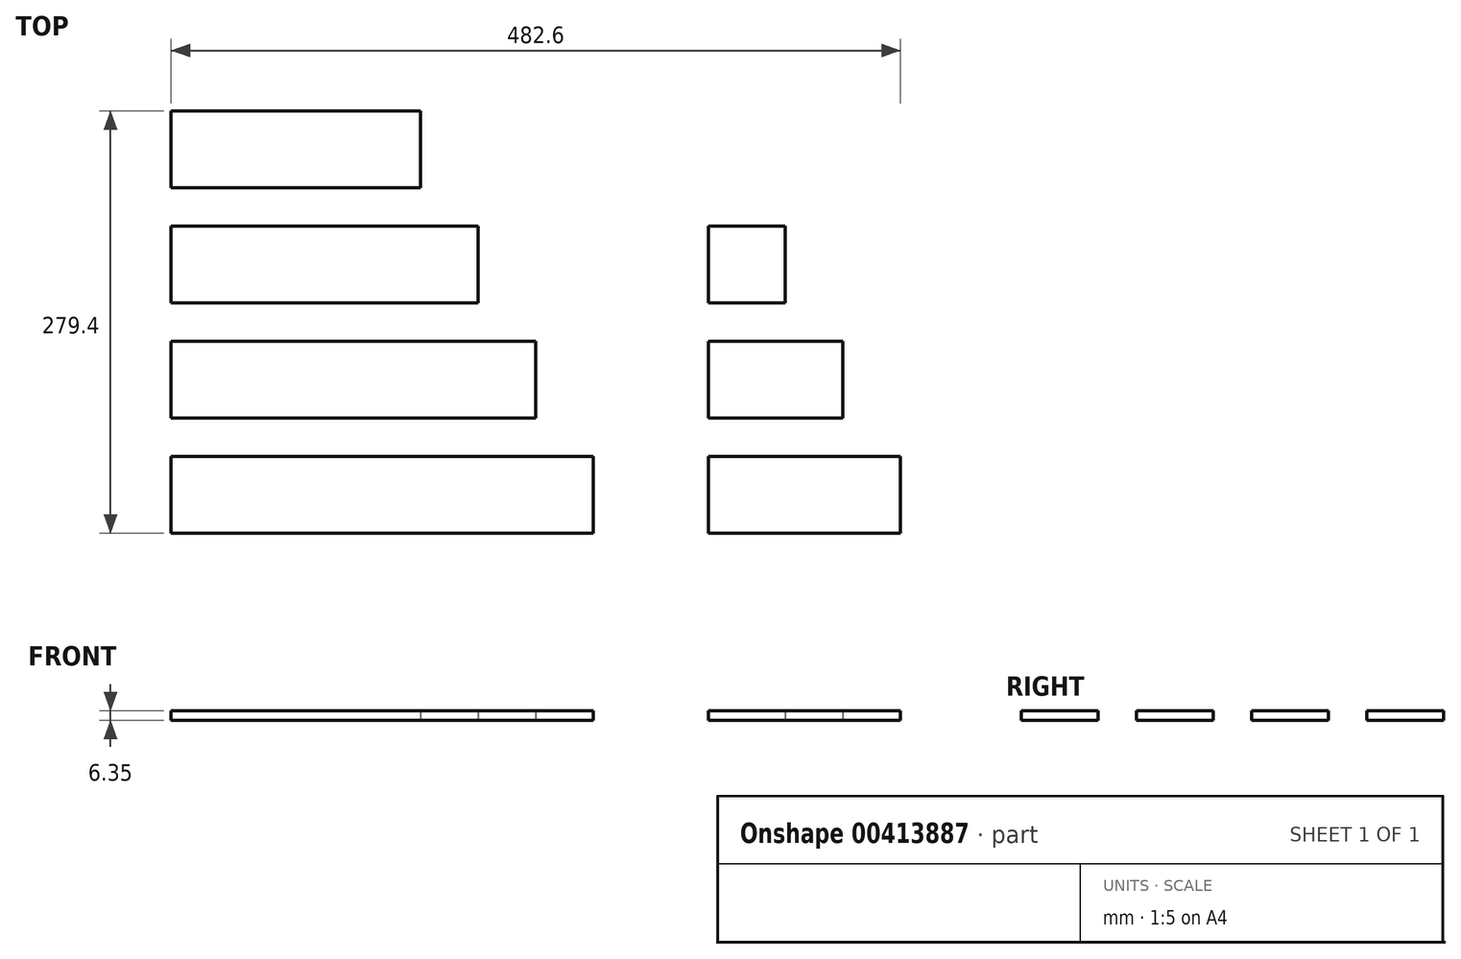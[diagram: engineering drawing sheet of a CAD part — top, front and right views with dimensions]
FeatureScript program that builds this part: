
annotation { "Feature Type Name" : "Feature", "Feature Type Description" : "" }
export const myFeature = defineFeature(function(context is Context, id is Id, definition is map)
    precondition{}
    {
        {
            var Q0;
            Q0=qCreatedBy(makeId("Top.planeOp"),FACE);
            var sketch = newSketch(context, id + "F0", { "sketchPlane" : qUnion([Q0])});
            skLineSegment(sketch, "E0.bottom", {"start": v(0, 38.1) * mm, "end": v(266.7, 38.1) * mm});
            skLineSegment(sketch, "E0.top", {"start": v(0, 0) * mm, "end": v(266.7, 0) * mm});
            skLineSegment(sketch, "E0.left", {"start": v(0, 38.1) * mm, "end": v(0, 0) * mm});
            skLineSegment(sketch, "E0.right", {"start": v(266.7, 38.1) * mm, "end": v(266.7, 0) * mm});
            skLineSegment(sketch, "E1.bottom", {"start": v(0, 76.2) * mm, "end": v(228.6, 76.2) * mm});
            skLineSegment(sketch, "E1.top", {"start": v(0, 114.3) * mm, "end": v(228.6, 114.3) * mm});
            skLineSegment(sketch, "E1.left", {"start": v(0, 76.2) * mm, "end": v(0, 114.3) * mm});
            skLineSegment(sketch, "E1.right", {"start": v(228.6, 76.2) * mm, "end": v(228.6, 114.3) * mm});
            skLineSegment(sketch, "E2.bottom", {"start": v(0, 152.4) * mm, "end": v(190.5, 152.4) * mm});
            skLineSegment(sketch, "E2.top", {"start": v(0, 190.5) * mm, "end": v(190.5, 190.5) * mm});
            skLineSegment(sketch, "E2.left", {"start": v(0, 152.4) * mm, "end": v(0, 190.5) * mm});
            skLineSegment(sketch, "E2.right", {"start": v(190.5, 152.4) * mm, "end": v(190.5, 190.5) * mm});
            skLineSegment(sketch, "E3.bottom", {"start": v(0, 228.6) * mm, "end": v(152.4, 228.6) * mm});
            skLineSegment(sketch, "E3.top", {"start": v(0, 266.7) * mm, "end": v(152.4, 266.7) * mm});
            skLineSegment(sketch, "E3.left", {"start": v(0, 228.6) * mm, "end": v(0, 266.7) * mm});
            skLineSegment(sketch, "E3.right", {"start": v(152.4, 228.6) * mm, "end": v(152.4, 266.7) * mm});
            skLineSegment(sketch, "E4.bottom", {"start": v(355.6, 0) * mm, "end": v(469.9, 0) * mm});
            skLineSegment(sketch, "E4.top", {"start": v(355.6, 38.1) * mm, "end": v(469.9, 38.1) * mm});
            skLineSegment(sketch, "E4.left", {"start": v(355.6, 0) * mm, "end": v(355.6, 38.1) * mm});
            skLineSegment(sketch, "E4.right", {"start": v(469.9, 0) * mm, "end": v(469.9, 38.1) * mm});
            skLineSegment(sketch, "E5.bottom", {"start": v(355.6, 76.2) * mm, "end": v(431.8, 76.2) * mm});
            skLineSegment(sketch, "E5.top", {"start": v(355.6, 114.3) * mm, "end": v(431.8, 114.3) * mm});
            skLineSegment(sketch, "E5.left", {"start": v(355.6, 76.2) * mm, "end": v(355.6, 114.3) * mm});
            skLineSegment(sketch, "E5.right", {"start": v(431.8, 76.2) * mm, "end": v(431.8, 114.3) * mm});
            skLineSegment(sketch, "E6.bottom", {"start": v(355.6, 152.4) * mm, "end": v(393.7, 152.4) * mm});
            skLineSegment(sketch, "E6.top", {"start": v(355.6, 190.5) * mm, "end": v(393.7, 190.5) * mm});
            skLineSegment(sketch, "E6.left", {"start": v(355.6, 152.4) * mm, "end": v(355.6, 190.5) * mm});
            skLineSegment(sketch, "E6.right", {"start": v(393.7, 152.4) * mm, "end": v(393.7, 190.5) * mm});
            skLineSegment(sketch, "E7.0", {"start": v(-6.35, -6.35) * mm, "end": v(273.05, -6.35) * mm});
            skLineSegment(sketch, "E7.1", {"start": v(-6.35, 44.45) * mm, "end": v(-6.35, -6.35) * mm});
            skLineSegment(sketch, "E7.2", {"start": v(-6.35, 44.45) * mm, "end": v(273.05, 44.45) * mm});
            skLineSegment(sketch, "E7.3", {"start": v(273.05, 44.45) * mm, "end": v(273.05, -6.35) * mm});
            skLineSegment(sketch, "E8.0", {"start": v(-6.35, 69.85) * mm, "end": v(234.95, 69.85) * mm});
            skLineSegment(sketch, "E8.1", {"start": v(-6.35, 69.85) * mm, "end": v(-6.35, 120.65) * mm});
            skLineSegment(sketch, "E8.2", {"start": v(-6.35, 120.65) * mm, "end": v(234.95, 120.65) * mm});
            skLineSegment(sketch, "E8.3", {"start": v(234.95, 69.85) * mm, "end": v(234.95, 120.65) * mm});
            skLineSegment(sketch, "E9.0", {"start": v(196.85, 146.05) * mm, "end": v(196.85, 196.85) * mm});
            skLineSegment(sketch, "E9.1", {"start": v(-6.35, 146.05) * mm, "end": v(196.85, 146.05) * mm});
            skLineSegment(sketch, "E9.2", {"start": v(-6.35, 146.05) * mm, "end": v(-6.35, 196.85) * mm});
            skLineSegment(sketch, "E9.3", {"start": v(-6.35, 196.85) * mm, "end": v(196.85, 196.85) * mm});
            skLineSegment(sketch, "E10.0", {"start": v(-6.35, 222.25) * mm, "end": v(158.75, 222.25) * mm});
            skLineSegment(sketch, "E10.1", {"start": v(-6.35, 222.25) * mm, "end": v(-6.35, 273.05) * mm});
            skLineSegment(sketch, "E10.2", {"start": v(-6.35, 273.05) * mm, "end": v(158.75, 273.05) * mm});
            skLineSegment(sketch, "E10.3", {"start": v(158.75, 222.25) * mm, "end": v(158.75, 273.05) * mm});
            skLineSegment(sketch, "E11.0", {"start": v(400.05, 146.05) * mm, "end": v(400.05, 196.85) * mm});
            skLineSegment(sketch, "E11.1", {"start": v(349.25, 146.05) * mm, "end": v(400.05, 146.05) * mm});
            skLineSegment(sketch, "E11.2", {"start": v(349.25, 146.05) * mm, "end": v(349.25, 196.85) * mm});
            skLineSegment(sketch, "E11.3", {"start": v(349.25, 196.85) * mm, "end": v(400.05, 196.85) * mm});
            skLineSegment(sketch, "E12.0", {"start": v(349.25, 69.85) * mm, "end": v(438.15, 69.85) * mm});
            skLineSegment(sketch, "E12.1", {"start": v(349.25, 69.85) * mm, "end": v(349.25, 120.65) * mm});
            skLineSegment(sketch, "E12.2", {"start": v(349.25, 120.65) * mm, "end": v(438.15, 120.65) * mm});
            skLineSegment(sketch, "E12.3", {"start": v(438.15, 69.85) * mm, "end": v(438.15, 120.65) * mm});
            skLineSegment(sketch, "E13.0", {"start": v(349.25, -6.35) * mm, "end": v(476.25, -6.35) * mm});
            skLineSegment(sketch, "E13.1", {"start": v(349.25, -6.35) * mm, "end": v(349.25, 44.45) * mm});
            skLineSegment(sketch, "E13.2", {"start": v(349.25, 44.45) * mm, "end": v(476.25, 44.45) * mm});
            skLineSegment(sketch, "E13.3", {"start": v(476.25, -6.35) * mm, "end": v(476.25, 44.45) * mm});
            skSolve(sketch);
        }
        {
            var Q0;
            Q0 = qSketchRegion(id + "F0", true);
            var Q1;
            Q1=makeQuery(id+"F0.imprint","IMPRINT",FACE,{"disambiguationData":[TD([[makeQuery(id+"F0.imprint","IMPRINT",EDGE,{"derivedFrom":sQuery(id+"F0.wireOp",EDGE,"E3.bottom")}),1.0]])]});
            var Q2;
            Q2=makeQuery(id+"F0.imprint","IMPRINT",FACE,{"disambiguationData":[TD([[makeQuery(id+"F0.imprint","IMPRINT",EDGE,{"derivedFrom":sQuery(id+"F0.wireOp",EDGE,"E2.bottom")}),1.0]])]});
            var Q3;
            Q3=makeQuery(id+"F0.imprint","IMPRINT",FACE,{"disambiguationData":[TD([[makeQuery(id+"F0.imprint","IMPRINT",EDGE,{"derivedFrom":sQuery(id+"F0.wireOp",EDGE,"E1.bottom")}),1.0]])]});
            var Q4;
            Q4=makeQuery(id+"F0.imprint","IMPRINT",FACE,{"disambiguationData":[TD([[makeQuery(id+"F0.imprint","IMPRINT",EDGE,{"derivedFrom":sQuery(id+"F0.wireOp",EDGE,"E0.bottom")}),-1.0]])]});
            var Q5;
            Q5=makeQuery(id+"F0.imprint","IMPRINT",FACE,{"disambiguationData":[TD([[makeQuery(id+"F0.imprint","IMPRINT",EDGE,{"derivedFrom":sQuery(id+"F0.wireOp",EDGE,"E4.bottom")}),1.0]])]});
            var Q6;
            Q6=makeQuery(id+"F0.imprint","IMPRINT",FACE,{"disambiguationData":[TD([[makeQuery(id+"F0.imprint","IMPRINT",EDGE,{"derivedFrom":sQuery(id+"F0.wireOp",EDGE,"E5.bottom")}),1.0]])]});
            var Q7;
            Q7=makeQuery(id+"F0.imprint","IMPRINT",FACE,{"disambiguationData":[TD([[makeQuery(id+"F0.imprint","IMPRINT",EDGE,{"derivedFrom":sQuery(id+"F0.wireOp",EDGE,"E6.bottom")}),1.0]])]});
            extrude(context, id + "F1", {"entities" : qUnion([Q0, Q1, Q2, Q3, Q4, Q5, Q6, Q7]), "depth" : 6.35 * mm});
        }
    });
